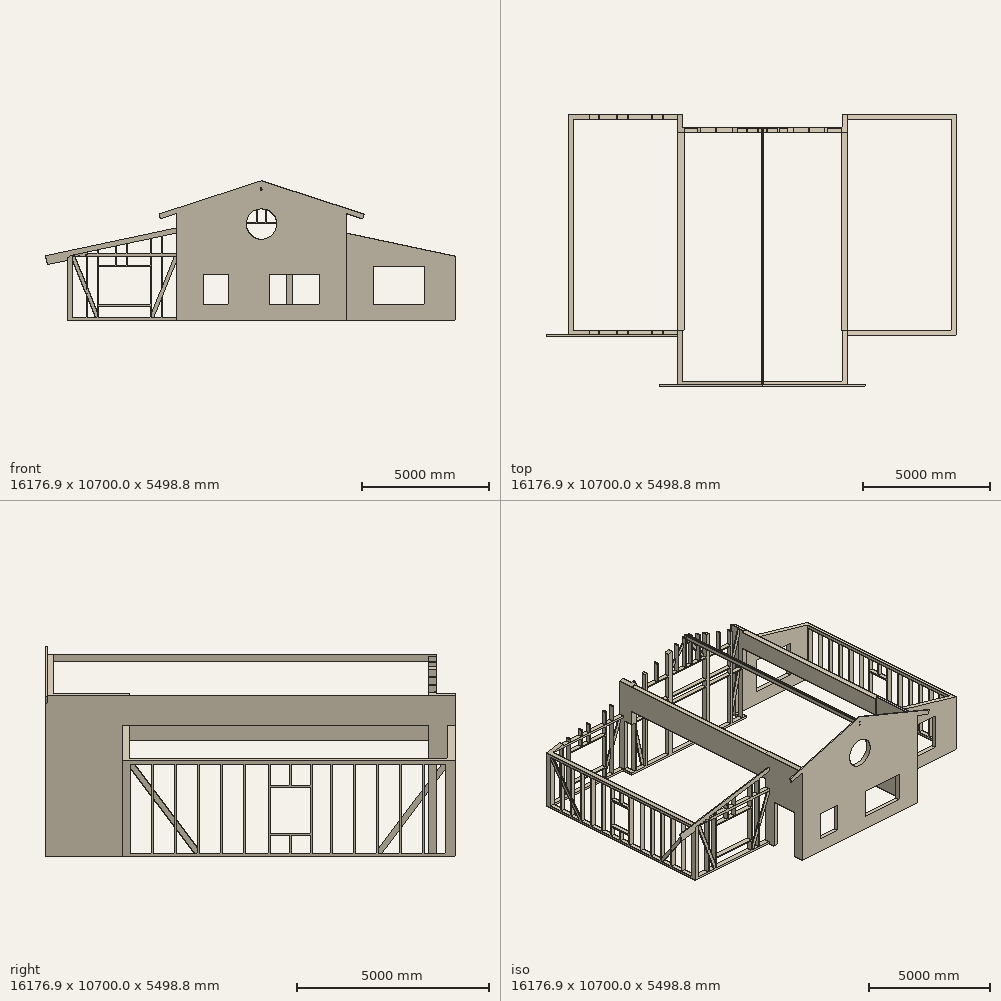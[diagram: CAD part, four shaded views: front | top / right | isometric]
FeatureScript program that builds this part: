
annotation { "Feature Type Name" : "Feature", "Feature Type Description" : "" }
export const myFeature = defineFeature(function(context is Context, id is Id, definition is map)
    precondition{}
    {
        {
            var Q0;
            Q0=qCreatedBy(makeId("Top.planeOp"),FACE);
            var sketch = newSketch(context, id + "F0", { "sketchPlane" : qUnion([Q0])});
            skLineSegment(sketch, "E0.bottom", {"start": v(-3150, 4900) * mm, "end": v(3150, 4900) * mm});
            skLineSegment(sketch, "E0.top", {"start": v(-3150, -4900) * mm, "end": v(3150, -4900) * mm});
            skPoint(sketch, "E0.middle", {"position": v(0, 0) * mm});
            skLineSegment(sketch, "E1.bottom", {"start": v(-3150, 5100) * mm, "end": v(3150, 5100) * mm});
            skLineSegment(sketch, "E1.top", {"start": v(-3350, -5100) * mm, "end": v(3350, -5100) * mm});
            skLineSegment(sketch, "E1.right", {"start": v(3350, 5100) * mm, "end": v(3350, 4900) * mm});
            skLineSegment(sketch, "E2.bottom", {"start": v(3350, -2900) * mm, "end": v(7450, -2900) * mm});
            skLineSegment(sketch, "E2.top", {"start": v(3350, 5400) * mm, "end": v(7450, 5400) * mm});
            skLineSegment(sketch, "E2.left", {"start": v(3350, 4900) * mm, "end": v(3350, 5400) * mm});
            skLineSegment(sketch, "E2.right", {"start": v(7450, -2900) * mm, "end": v(7450, 5400) * mm});
            skLineSegment(sketch, "E3.bottom", {"start": v(3350, -3100) * mm, "end": v(7650, -3100) * mm});
            skLineSegment(sketch, "E3.top", {"start": v(3150, 5600) * mm, "end": v(7650, 5600) * mm});
            skLineSegment(sketch, "E3.right", {"start": v(7650, -3100) * mm, "end": v(7650, 5600) * mm});
            skLineSegment(sketch, "E4.top", {"start": v(-3350, 5400) * mm, "end": v(-7450, 5400) * mm});
            skLineSegment(sketch, "E4.right", {"start": v(-7450, -2900) * mm, "end": v(-7450, 5400) * mm});
            skLineSegment(sketch, "E5.bottom", {"start": v(-3350, -3125) * mm, "end": v(-7650, -3125) * mm});
            skLineSegment(sketch, "E5.top", {"start": v(-3350, 5600) * mm, "end": v(-7650, 5600) * mm});
            skLineSegment(sketch, "E5.left", {"start": v(-3350, 4900) * mm, "end": v(-3350, 5100) * mm});
            skLineSegment(sketch, "E5.right", {"start": v(-7650, -3125) * mm, "end": v(-7650, 5600) * mm});
            skLineSegment(sketch, "E6.bottom", {"start": v(-3350, 5600) * mm, "end": v(-3150, 5600) * mm});
            skLineSegment(sketch, "E6.left", {"start": v(-3350, 5400) * mm, "end": v(-3350, 5100) * mm});
            skLineSegment(sketch, "E6.right", {"start": v(-3150, 5600) * mm, "end": v(-3150, 5100) * mm});
            skLineSegment(sketch, "E7.trimOffspring", {"start": v(3150, 5100) * mm, "end": v(3150, 5600) * mm});
            skLineSegment(sketch, "E8.trimOffspring", {"start": v(3350, -3100) * mm, "end": v(3350, -5100) * mm});
            skLineSegment(sketch, "E9.trimOffspring", {"start": v(-3350, -3125) * mm, "end": v(-3350, -5100) * mm});
            skLineSegment(sketch, "E10", {"start": v(-3350, -2900) * mm, "end": v(-7450, -2900) * mm});
            skLineSegment(sketch, "E11", {"start": v(-3350, 4900) * mm, "end": v(-3150, 4900) * mm});
            skLineSegment(sketch, "E12", {"start": v(3150, 4900) * mm, "end": v(3350, 4900) * mm});
            skLineSegment(sketch, "E13", {"start": v(-3350, -2900) * mm, "end": v(-3150, -2900) * mm});
            skLineSegment(sketch, "E14", {"start": v(-3150, -2900) * mm, "end": v(-3150, -4900) * mm});
            skLineSegment(sketch, "E15", {"start": v(3150, -4900) * mm, "end": v(3150, -2900) * mm});
            skLineSegment(sketch, "E16", {"start": v(3150, -2900) * mm, "end": v(3350, -2900) * mm});
            skSolve(sketch);
        }
        {
            var Q0;
            Q0=qSketchRegion(id+"F0",true);
            extrude(context, id + "F1", {"entities" : qUnion([Q0]), "depth" : 5330 * mm});
        }
        {
            var Q0;
            Q0=makeQuery(id+"F1.opExtrude","SWEPT_FACE",FACE,{"disambiguationData":[OSD([sQuery(id+"F0.wireOp",EDGE,"E1.top")])]});
            var sketch = newSketch(context, id + "F2", { "sketchPlane" : qUnion([Q0])});
            skLineSegment(sketch, "E17.top", {"start": v(0, 6465.16) * mm, "end": v(-7750, 6465.16) * mm});
            skLineSegment(sketch, "E17.left", {"start": v(0, 5288.48) * mm, "end": v(0, 5330) * mm});
            skLineSegment(sketch, "E17.right", {"start": v(-7750, 2500) * mm, "end": v(-7750, 6465.16) * mm});
            skLineSegment(sketch, "E18.top", {"start": v(0, 6465.16) * mm, "end": v(7750, 6465.16) * mm});
            skLineSegment(sketch, "E18.right", {"start": v(7750, 2500) * mm, "end": v(7750, 6465.16) * mm});
            skLineSegment(sketch, "E19.bottom", {"start": v(0, 0) * mm, "end": v(-3350, 0) * mm});
            skLineSegment(sketch, "E19.right", {"start": v(-3350, 3435.25) * mm, "end": v(-3350, 4200) * mm});
            skLineSegment(sketch, "E20.right", {"start": v(3350, 3435.25) * mm, "end": v(3350, 4200) * mm});
            skLineSegment(sketch, "E21", {"start": v(-3350, 4200) * mm, "end": v(0, 5288.48) * mm});
            skLineSegment(sketch, "E22", {"start": v(0, 5288.48) * mm, "end": v(3350, 4200) * mm});
            skPoint(sketch, "E23.orphan", {"position": v(-7750, 0) * mm});
            skLineSegment(sketch, "E24", {"start": v(-7750, 2500) * mm, "end": v(-3350, 3435.25) * mm});
            skLineSegment(sketch, "E25", {"start": v(3350, 3435.25) * mm, "end": v(7750, 2500) * mm});
            skPoint(sketch, "E26.orphan", {"position": v(-7750, 2100) * mm});
            skPoint(sketch, "E27.orphan", {"position": v(-3350, 3024.62) * mm});
            skPoint(sketch, "E28.orphan", {"position": v(7750, 2100) * mm});
            skPoint(sketch, "E29.orphan", {"position": v(3350, 3024.62) * mm});
            skSolve(sketch);
        }
        {
            var Q0;
            Q0=qSketchRegion(id+"F2",true);
            extrude(context, id + "F3", {"entities" : qUnion([Q0]), "operationType" : NewBodyOperationType.REMOVE, "endBound" : BoundingType.THROUGH_ALL, "oppositeDirection" : true, "depth" : 25 * mm});
        }
        {
            var Q0;
            Q0=makeQuery(id+"F3.boolean.opBoolean","MERGE",FACE,{"derivedFrom":[makeQuery(id+"F1.opExtrude","SWEPT_FACE",FACE,{"disambiguationData":[OSD([sQuery(id+"F0.wireOp",EDGE,"E5.left"),sQuery(id+"F0.wireOp",EDGE,"E6.left")])]}),makeQuery(id+"F3.opExtrude","SWEPT_FACE",FACE,{"disambiguationData":[OSD([sQuery(id+"F2.wireOp",EDGE,"E19.right")])]})]});
            var sketch = newSketch(context, id + "F4", { "sketchPlane" : qUnion([Q0])});
            skLineSegment(sketch, "E30.bottom", {"start": v(-4900, 4200) * mm, "end": v(2900, 4200) * mm});
            skLineSegment(sketch, "E30.left", {"start": v(-4900, 4200) * mm, "end": v(-4900, 3147.99) * mm});
            skLineSegment(sketch, "E30.right", {"start": v(2900, 4200) * mm, "end": v(2900, 3147.99) * mm});
            skLineSegment(sketch, "E31.right", {"start": v(-4900, 3024.62) * mm, "end": v(-4900, 3147.99) * mm});
            skLineSegment(sketch, "E32.bottom", {"start": v(-4900, 3024.62) * mm, "end": v(2900, 3024.62) * mm});
            skLineSegment(sketch, "E32.right", {"start": v(2900, 3024.62) * mm, "end": v(2900, 3147.99) * mm});
            skSolve(sketch);
        }
        {
            var Q0;
            Q0=qSketchRegion(id+"F4",true);
            extrude(context, id + "F5", {"entities" : qUnion([Q0]), "operationType" : NewBodyOperationType.ADD, "oppositeDirection" : true, "depth" : 250 * mm});
        }
        {
            var Q0;
            Q0=makeQuery(id+"F3.boolean.opBoolean","MERGE",FACE,{"derivedFrom":[makeQuery(id+"F1.opExtrude","SWEPT_FACE",FACE,{"disambiguationData":[OSD([sQuery(id+"F0.wireOp",EDGE,"E8.trimOffspring")])]}),makeQuery(id+"F3.opExtrude","SWEPT_FACE",FACE,{"disambiguationData":[OSD([sQuery(id+"F2.wireOp",EDGE,"E20.right")])]})]});
            var sketch = newSketch(context, id + "F6", { "sketchPlane" : qUnion([Q0])});
            skLineSegment(sketch, "E33.bottom", {"start": v(-2900, 4200) * mm, "end": v(4900, 4200) * mm});
            skLineSegment(sketch, "E33.top", {"start": v(-2900, 3435.25) * mm, "end": v(4900, 3435.25) * mm});
            skLineSegment(sketch, "E33.left", {"start": v(-2900, 4200) * mm, "end": v(-2900, 3435.25) * mm});
            skLineSegment(sketch, "E33.right", {"start": v(4900, 4200) * mm, "end": v(4900, 3435.25) * mm});
            skSolve(sketch);
        }
        {
            var Q0;
            Q0=qSketchRegion(id+"F6",true);
            extrude(context, id + "F7", {"entities" : qUnion([Q0]), "operationType" : NewBodyOperationType.ADD, "oppositeDirection" : true, "depth" : 250 * mm});
        }
        {
            var Q0;
            Q0=makeQuery(id+"F1.opExtrude","SWEPT_FACE",FACE,{"disambiguationData":[OSD([sQuery(id+"F0.wireOp",EDGE,"E5.bottom")])]});
            var sketch = newSketch(context, id + "F8", { "sketchPlane" : qUnion([Q0])});
            skLineSegment(sketch, "E34.bottom", {"start": v(-6420, 2100) * mm, "end": v(-4380, 2100) * mm});
            skLineSegment(sketch, "E34.top", {"start": v(-6420, 600) * mm, "end": v(-4380, 600) * mm});
            skLineSegment(sketch, "E34.left", {"start": v(-6420, 2100) * mm, "end": v(-6420, 600) * mm});
            skLineSegment(sketch, "E34.right", {"start": v(-4380, 2100) * mm, "end": v(-4380, 600) * mm});
            skLineSegment(sketch, "E35.bottom", {"start": v(4420, 2100) * mm, "end": v(6420, 2100) * mm});
            skLineSegment(sketch, "E35.top", {"start": v(4420, 600) * mm, "end": v(6420, 600) * mm});
            skLineSegment(sketch, "E35.left", {"start": v(4420, 2100) * mm, "end": v(4420, 600) * mm});
            skLineSegment(sketch, "E35.right", {"start": v(6420, 2100) * mm, "end": v(6420, 600) * mm});
            skSolve(sketch);
        }
        {
            var Q0;
            Q0=qSketchRegion(id+"F8",true);
            extrude(context, id + "F9", {"entities" : qUnion([Q0]), "operationType" : NewBodyOperationType.REMOVE, "endBound" : BoundingType.THROUGH_ALL, "oppositeDirection" : true, "depth" : 25 * mm});
        }
        {
            var Q0;
            {var subQ0=makeQuery(id+"F3.opExtrude","SWEPT_FACE",FACE,{"disambiguationData":[OSD([sQuery(id+"F2.wireOp",EDGE,"E19.right")])]});Q0=makeQuery(id+"F5.boolean.opBoolean","MERGE",FACE,{"derivedFrom":[makeQuery(id+"F3.boolean.opBoolean","MERGE",FACE,{"derivedFrom":[makeQuery(id+"F1.opExtrude","SWEPT_FACE",FACE,{"disambiguationData":[OSD([sQuery(id+"F0.wireOp",EDGE,"E5.left"),sQuery(id+"F0.wireOp",EDGE,"E6.left")])]}),subQ0]}),makeQuery(id+"F3.boolean.opBoolean","MERGE",FACE,{"derivedFrom":[makeQuery(id+"F1.opExtrude","SWEPT_FACE",FACE,{"disambiguationData":[OSD([sQuery(id+"F0.wireOp",EDGE,"E9.trimOffspring")])]}),subQ0]}),makeQuery(id+"F5.opExtrude","CAP_FACE",FACE,{"disambiguationData":[OSD([sQuery(id+"F4.wireOp",EDGE,"E30.bottom"),sQuery(id+"F4.wireOp",EDGE,"E30.left"),sQuery(id+"F4.wireOp",EDGE,"E30.right"),sQuery(id+"F4.wireOp",EDGE,"E32.bottom"),sQuery(id+"F4.wireOp",EDGE,"E31.right"),sQuery(id+"F4.wireOp",EDGE,"E32.right")])],"isStart":true})]});}
            var sketch = newSketch(context, id + "F10", { "sketchPlane" : qUnion([Q0])});
            skLineSegment(sketch, "E36.bottom", {"start": v(4625, 0) * mm, "end": v(3425, 0) * mm});
            skLineSegment(sketch, "E36.top", {"start": v(4625, 2100) * mm, "end": v(3425, 2100) * mm});
            skLineSegment(sketch, "E36.left", {"start": v(4625, 0) * mm, "end": v(4625, 2100) * mm});
            skLineSegment(sketch, "E36.right", {"start": v(3425, 0) * mm, "end": v(3425, 2100) * mm});
            skSolve(sketch);
        }
        {
            var Q0;
            Q0=qSketchRegion(id+"F10",true);
            extrude(context, id + "F11", {"entities" : qUnion([Q0]), "operationType" : NewBodyOperationType.REMOVE, "oppositeDirection" : true, "depth" : 250 * mm});
        }
        {
            var Q0;
            Q0=makeQuery(id+"F1.opExtrude","SWEPT_FACE",FACE,{"disambiguationData":[OSD([sQuery(id+"F0.wireOp",EDGE,"E1.top")])]});
            var sketch = newSketch(context, id + "F12", { "sketchPlane" : qUnion([Q0])});
            skLineSegment(sketch, "E37.bottom", {"start": v(300, 1800) * mm, "end": v(2300, 1800) * mm});
            skLineSegment(sketch, "E37.top", {"start": v(300, 600) * mm, "end": v(2300, 600) * mm});
            skLineSegment(sketch, "E37.left", {"start": v(300, 1800) * mm, "end": v(300, 600) * mm});
            skLineSegment(sketch, "E37.right", {"start": v(2300, 1800) * mm, "end": v(2300, 600) * mm});
            skLineSegment(sketch, "E38.bottom", {"start": v(-1300, 600) * mm, "end": v(-2300, 600) * mm});
            skLineSegment(sketch, "E38.top", {"start": v(-1300, 1800) * mm, "end": v(-2300, 1800) * mm});
            skLineSegment(sketch, "E38.left", {"start": v(-1300, 600) * mm, "end": v(-1300, 1800) * mm});
            skLineSegment(sketch, "E38.right", {"start": v(-2300, 600) * mm, "end": v(-2300, 1800) * mm});
            skArc(sketch, "E39", {"start": v(-50, 4387.92) * mm, "mid": v(-424.26, 4214.27) * mm, "end": v(-597.91, 3840) * mm});
            skPoint(sketch, "E40.orphan", {"position": v(-1581.41, 3840) * mm});
            skPoint(sketch, "E41.orphan", {"position": v(-1581.41, 3740) * mm});
            skPoint(sketch, "E42.right.end.orphan", {"position": v(1581.41, 3840) * mm});
            skPoint(sketch, "E42.right.start.orphan", {"position": v(1581.41, 3740) * mm});
            skPoint(sketch, "E43.orphan", {"position": v(-50, 2853.08) * mm});
            skPoint(sketch, "E44.orphan", {"position": v(50, 2853.08) * mm});
            skPoint(sketch, "E45.orphan", {"position": v(-50, 4726.93) * mm});
            skPoint(sketch, "E46.orphan", {"position": v(50, 4726.93) * mm});
            skArc(sketch, "E47.trimOffspring", {"start": v(-597.91, 3740) * mm, "mid": v(-424.26, 3365.74) * mm, "end": v(-50, 3192.09) * mm});
            skArc(sketch, "E48.trimOffspring", {"start": v(597.91, 3840) * mm, "mid": v(424.26, 4214.27) * mm, "end": v(50, 4387.92) * mm});
            skArc(sketch, "E49.trimOffspring", {"start": v(50, 3192.09) * mm, "mid": v(424.26, 3365.74) * mm, "end": v(597.91, 3740) * mm});
            skCircle(sketch, "E50", {"center": v(0, 3790) * mm, "radius": 600 * mm});
            skSolve(sketch);
        }
        {
            var Q0;
            Q0=qSketchRegion(id+"F12",true);
            extrude(context, id + "F13", {"entities" : qUnion([Q0]), "operationType" : NewBodyOperationType.REMOVE, "oppositeDirection" : true, "depth" : 250 * mm});
        }
        {
            var Q0;
            Q0=makeQuery(id+"F1.opExtrude","SWEPT_FACE",FACE,{"disambiguationData":[OSD([sQuery(id+"F0.wireOp",EDGE,"E1.bottom")])]});
            var sketch = newSketch(context, id + "F14", { "sketchPlane" : qUnion([Q0])});
            skLineSegment(sketch, "E51.bottom", {"start": v(-1000, 0) * mm, "end": v(1000, 0) * mm});
            skLineSegment(sketch, "E51.top", {"start": v(-1000, 2400) * mm, "end": v(1000, 2400) * mm});
            skLineSegment(sketch, "E51.left", {"start": v(-1000, 0) * mm, "end": v(-1000, 2400) * mm});
            skLineSegment(sketch, "E51.right", {"start": v(1000, 0) * mm, "end": v(1000, 2400) * mm});
            skPoint(sketch, "E51.middle", {"position": v(0, 1200) * mm});
            skLineSegment(sketch, "E52.bottom", {"start": v(1200, 2400) * mm, "end": v(2450, 2400) * mm});
            skLineSegment(sketch, "E52.top", {"start": v(1200, 0) * mm, "end": v(2450, 0) * mm});
            skLineSegment(sketch, "E52.left", {"start": v(1200, 2400) * mm, "end": v(1200, 0) * mm});
            skLineSegment(sketch, "E52.right", {"start": v(2450, 2400) * mm, "end": v(2450, 0) * mm});
            skLineSegment(sketch, "E53.bottom", {"start": v(-1200, 2400) * mm, "end": v(-2450, 2400) * mm});
            skLineSegment(sketch, "E53.top", {"start": v(-1200, 0) * mm, "end": v(-2450, 0) * mm});
            skLineSegment(sketch, "E53.left", {"start": v(-1200, 2400) * mm, "end": v(-1200, 0) * mm});
            skLineSegment(sketch, "E53.right", {"start": v(-2450, 2400) * mm, "end": v(-2450, 0) * mm});
            skLineSegment(sketch, "E54.bottom", {"start": v(-2450, 2800) * mm, "end": v(-1200, 2800) * mm});
            skLineSegment(sketch, "E54.top", {"start": v(-2450, 3800) * mm, "end": v(-1200, 3800) * mm});
            skLineSegment(sketch, "E54.left", {"start": v(-2450, 2800) * mm, "end": v(-2450, 3800) * mm});
            skLineSegment(sketch, "E54.right", {"start": v(-1200, 2800) * mm, "end": v(-1200, 3800) * mm});
            skLineSegment(sketch, "E55.bottom", {"start": v(-1000, 2800) * mm, "end": v(1000, 2800) * mm});
            skLineSegment(sketch, "E55.top", {"start": v(-1000, 3800) * mm, "end": v(1000, 3800) * mm});
            skLineSegment(sketch, "E55.left", {"start": v(-1000, 2800) * mm, "end": v(-1000, 3800) * mm});
            skLineSegment(sketch, "E55.right", {"start": v(1000, 2800) * mm, "end": v(1000, 3800) * mm});
            skLineSegment(sketch, "E56.bottom", {"start": v(1200, 2800) * mm, "end": v(2450, 2800) * mm});
            skLineSegment(sketch, "E56.top", {"start": v(1200, 3800) * mm, "end": v(2450, 3800) * mm});
            skLineSegment(sketch, "E56.left", {"start": v(1200, 2800) * mm, "end": v(1200, 3800) * mm});
            skLineSegment(sketch, "E56.right", {"start": v(2450, 2800) * mm, "end": v(2450, 3800) * mm});
            skSolve(sketch);
        }
        {
            var Q0;
            Q0=qSketchRegion(id+"F14",true);
            extrude(context, id + "F15", {"entities" : qUnion([Q0]), "operationType" : NewBodyOperationType.REMOVE, "oppositeDirection" : true, "depth" : 250 * mm});
        }
        {
            var Q0;
            Q0=makeQuery(id+"F1.opExtrude","SWEPT_FACE",FACE,{"disambiguationData":[OSD([sQuery(id+"F0.wireOp",EDGE,"E3.right")])]});
            var sketch = newSketch(context, id + "F16", { "sketchPlane" : qUnion([Q0])});
            skLineSegment(sketch, "E57.bottom", {"start": v(772.72, 1800) * mm, "end": v(1812.72, 1800) * mm});
            skLineSegment(sketch, "E57.top", {"start": v(772.72, 600) * mm, "end": v(1812.72, 600) * mm});
            skLineSegment(sketch, "E57.left", {"start": v(772.72, 1800) * mm, "end": v(772.72, 600) * mm});
            skLineSegment(sketch, "E57.right", {"start": v(1812.72, 1800) * mm, "end": v(1812.72, 600) * mm});
            skSolve(sketch);
        }
        {
            var Q0;
            Q0=qSketchRegion(id+"F16",true);
            extrude(context, id + "F17", {"entities" : qUnion([Q0]), "operationType" : NewBodyOperationType.REMOVE, "endBound" : BoundingType.THROUGH_ALL, "oppositeDirection" : true, "depth" : 25 * mm});
        }
        {
            var Q0;
            Q0=makeQuery(id+"F1.opExtrude","SWEPT_FACE",FACE,{"disambiguationData":[OSD([sQuery(id+"F0.wireOp",EDGE,"E5.bottom")])]});
            var sketch = newSketch(context, id + "F18", { "sketchPlane" : qUnion([Q0])});
            skLineSegment(sketch, "E58", {"start": v(-3350, 3435.25) * mm, "end": v(-8485.27, 2343.71) * mm});
            skLineSegment(sketch, "E59", {"start": v(-8485.27, 2343.71) * mm, "end": v(-8526.86, 2539.34) * mm});
            skLineSegment(sketch, "E60", {"start": v(-8526.86, 2539.34) * mm, "end": v(-3350, 3639.72) * mm});
            skLineSegment(sketch, "E61", {"start": v(-3350, 3639.72) * mm, "end": v(-3350, 3435.25) * mm});
            skLineSegment(sketch, "E62", {"start": v(-8485.27, 2343.71) * mm, "end": v(-8452, 2187.2) * mm});
            skLineSegment(sketch, "E63", {"start": v(-8452, 2187.2) * mm, "end": v(-3350, 3271.67) * mm});
            skLineSegment(sketch, "E64", {"start": v(-3350, 3271.67) * mm, "end": v(-3350, 3435.25) * mm});
            skSolve(sketch);
        }
        {
            var Q0;
            Q0=qSketchRegion(id+"F18",true);
            extrude(context, id + "F19", {"entities" : qUnion([Q0]), "oppositeDirection" : true, "depth" : 50 * mm});
        }
        {
            var Q0;
            Q0=makeQuery(id+"F3.boolean.opBoolean","COPY",FACE,{"disambiguationData":[TD([makeQuery(id+"F1.opExtrude","SWEPT_FACE",FACE,{"disambiguationData":[OSD([sQuery(id+"F0.wireOp",EDGE,"E0.top")])]})])],"derivedFrom":makeQuery(id+"F3.opExtrude","SWEPT_FACE",FACE,{"disambiguationData":[OSD([sQuery(id+"F2.wireOp",EDGE,"E21")])]})});
            var sketch = newSketch(context, id + "F20", { "sketchPlane" : qUnion([Q0])});
            skPoint(sketch, "E65.right.end.orphan", {"position": v(-2565.77, -4900) * mm});
            skLineSegment(sketch, "E66.bottom", {"start": v(1634.23, -5100) * mm, "end": v(-2565.77, -5100) * mm});
            skLineSegment(sketch, "E66.top", {"start": v(1634.23, -5050) * mm, "end": v(-2565.77, -5050) * mm});
            skLineSegment(sketch, "E66.left", {"start": v(1634.23, -5100) * mm, "end": v(1634.23, -5050) * mm});
            skLineSegment(sketch, "E66.right", {"start": v(-2565.77, -5100) * mm, "end": v(-2565.77, -5050) * mm});
            skSolve(sketch);
        }
        {
            var Q0;
            Q0=qSketchRegion(id+"F20",true);
            extrude(context, id + "F21", {"entities" : qUnion([Q0]), "depth" : 200 * mm});
        }
        {
            var Q0;
            Q0=makeQuery(id+"F3.boolean.opBoolean","COPY",FACE,{"disambiguationData":[TD([makeQuery(id+"F1.opExtrude","SWEPT_FACE",FACE,{"disambiguationData":[OSD([sQuery(id+"F0.wireOp",EDGE,"E0.top")])]})])],"derivedFrom":makeQuery(id+"F3.opExtrude","SWEPT_FACE",FACE,{"disambiguationData":[OSD([sQuery(id+"F2.wireOp",EDGE,"E22")])]})});
            var sketch = newSketch(context, id + "F22", { "sketchPlane" : qUnion([Q0])});
            skLineSegment(sketch, "E67.bottom", {"start": v(-1634.23, -5100) * mm, "end": v(2565.77, -5100) * mm});
            skLineSegment(sketch, "E67.top", {"start": v(-1634.23, -5050) * mm, "end": v(2565.77, -5050) * mm});
            skLineSegment(sketch, "E67.left", {"start": v(-1634.23, -5100) * mm, "end": v(-1634.23, -5050) * mm});
            skLineSegment(sketch, "E67.right", {"start": v(2565.77, -5100) * mm, "end": v(2565.77, -5050) * mm});
            skSolve(sketch);
        }
        {
            var Q0;
            Q0=qSketchRegion(id+"F22",true);
            extrude(context, id + "F23", {"entities" : qUnion([Q0]), "depth" : 200 * mm});
        }
        {
            var Q0;
            Q0=makeQuery(id+"F1.opExtrude","SWEPT_FACE",FACE,{"disambiguationData":[OSD([sQuery(id+"F0.wireOp",EDGE,"E5.right")])]});
            var sketch = newSketch(context, id + "F24", { "sketchPlane" : qUnion([Q0])});
            skLineSegment(sketch, "E68.bottom", {"start": v(-5350, 2421.26) * mm, "end": v(-4800, 2421.26) * mm});
            skLineSegment(sketch, "E68.top", {"start": v(-5350, 100) * mm, "end": v(-4800, 100) * mm});
            skLineSegment(sketch, "E68.left", {"start": v(-5350, 2421.26) * mm, "end": v(-5350, 100) * mm});
            skLineSegment(sketch, "E68.right", {"start": v(-1862.72, 2421.26) * mm, "end": v(-1862.72, 100) * mm});
            skPoint(sketch, "E69.firstSnap0", {"position": v(-3606.36, 2421.26) * mm});
            skLineSegment(sketch, "E69.bottom", {"start": v(-722.72, 2421.26) * mm, "end": v(-125, 2421.26) * mm});
            skLineSegment(sketch, "E69.top", {"start": v(-722.72, 100) * mm, "end": v(-125, 100) * mm});
            skLineSegment(sketch, "E69.left", {"start": v(-722.72, 2421.26) * mm, "end": v(-722.72, 100) * mm});
            skLineSegment(sketch, "E69.right", {"start": v(2875, 2421.26) * mm, "end": v(2875, 100) * mm});
            skLineSegment(sketch, "E70.bottom", {"start": v(-1812.72, 2421.26) * mm, "end": v(-1317.72, 2421.26) * mm});
            skLineSegment(sketch, "E70.top", {"start": v(-1812.72, 1850) * mm, "end": v(-1317.72, 1850) * mm});
            skLineSegment(sketch, "E70.left", {"start": v(-1812.72, 2421.26) * mm, "end": v(-1812.72, 1850) * mm});
            skLineSegment(sketch, "E70.right", {"start": v(-772.72, 2421.26) * mm, "end": v(-772.72, 1850) * mm});
            skLineSegment(sketch, "E71.bottom", {"start": v(-1812.72, 550) * mm, "end": v(-1317.72, 550) * mm});
            skLineSegment(sketch, "E71.top", {"start": v(-1812.72, 100) * mm, "end": v(-1317.72, 100) * mm});
            skLineSegment(sketch, "E71.left", {"start": v(-1812.72, 550) * mm, "end": v(-1812.72, 100) * mm});
            skLineSegment(sketch, "E71.right", {"start": v(-772.72, 550) * mm, "end": v(-772.72, 100) * mm});
            skLineSegment(sketch, "E72.left", {"start": v(-4800, 2421.26) * mm, "end": v(-4800, 100) * mm});
            skLineSegment(sketch, "E72.right", {"start": v(-4750, 2421.26) * mm, "end": v(-4750, 100) * mm});
            skLineSegment(sketch, "E73.left", {"start": v(-4200, 2421.26) * mm, "end": v(-4200, 100) * mm});
            skLineSegment(sketch, "E73.right", {"start": v(-4150, 2421.26) * mm, "end": v(-4150, 100) * mm});
            skLineSegment(sketch, "E74.bottom", {"start": v(-3606.36, 2421.26) * mm, "end": v(-3600, 2421.26) * mm});
            skLineSegment(sketch, "E74.left", {"start": v(-3600, 2421.26) * mm, "end": v(-3600, 100) * mm});
            skLineSegment(sketch, "E74.right", {"start": v(-3550, 2421.26) * mm, "end": v(-3550, 100) * mm});
            skLineSegment(sketch, "E75.left", {"start": v(-3000, 2421.26) * mm, "end": v(-3000, 100) * mm});
            skLineSegment(sketch, "E75.right", {"start": v(-2950, 2421.26) * mm, "end": v(-2950, 100) * mm});
            skLineSegment(sketch, "E76.left", {"start": v(-2400, 2421.26) * mm, "end": v(-2400, 100) * mm});
            skLineSegment(sketch, "E76.right", {"start": v(-2350, 2421.26) * mm, "end": v(-2350, 100) * mm});
            skLineSegment(sketch, "E77.trimOffspring", {"start": v(-4750, 2421.26) * mm, "end": v(-4200, 2421.26) * mm});
            skLineSegment(sketch, "E78.trimOffspring", {"start": v(-4150, 2421.26) * mm, "end": v(-3606.36, 2421.26) * mm});
            skLineSegment(sketch, "E79.trimOffspring", {"start": v(-3550, 2421.26) * mm, "end": v(-3000, 2421.26) * mm});
            skLineSegment(sketch, "E80.trimOffspring", {"start": v(-2950, 2421.26) * mm, "end": v(-2400, 2421.26) * mm});
            skLineSegment(sketch, "E81.trimOffspring", {"start": v(-2350, 2421.26) * mm, "end": v(-1862.72, 2421.26) * mm});
            skLineSegment(sketch, "E82.trimOffspring", {"start": v(-4750, 100) * mm, "end": v(-4200, 100) * mm});
            skLineSegment(sketch, "E83.trimOffspring", {"start": v(-4150, 100) * mm, "end": v(-3600, 100) * mm});
            skLineSegment(sketch, "E84.trimOffspring", {"start": v(-3550, 100) * mm, "end": v(-3000, 100) * mm});
            skLineSegment(sketch, "E85.trimOffspring", {"start": v(-2950, 100) * mm, "end": v(-2400, 100) * mm});
            skLineSegment(sketch, "E86.trimOffspring", {"start": v(-2350, 100) * mm, "end": v(-1862.72, 100) * mm});
            skLineSegment(sketch, "E87.left", {"start": v(-125, 2421.26) * mm, "end": v(-125, 100) * mm});
            skLineSegment(sketch, "E87.right", {"start": v(-75, 2421.26) * mm, "end": v(-75, 100) * mm});
            skLineSegment(sketch, "E88.left", {"start": v(475, 2421.26) * mm, "end": v(475, 100) * mm});
            skLineSegment(sketch, "E88.right", {"start": v(525, 2421.26) * mm, "end": v(525, 100) * mm});
            skLineSegment(sketch, "E89.left", {"start": v(1075, 2421.26) * mm, "end": v(1075, 100) * mm});
            skLineSegment(sketch, "E89.right", {"start": v(1125, 2421.26) * mm, "end": v(1125, 100) * mm});
            skLineSegment(sketch, "E90.left", {"start": v(1675, 2421.26) * mm, "end": v(1675, 100) * mm});
            skLineSegment(sketch, "E90.right", {"start": v(1725, 2421.26) * mm, "end": v(1725, 100) * mm});
            skLineSegment(sketch, "E91.left", {"start": v(2275, 2421.26) * mm, "end": v(2275, 100) * mm});
            skLineSegment(sketch, "E91.right", {"start": v(2325, 2421.26) * mm, "end": v(2325, 100) * mm});
            skLineSegment(sketch, "E92.trimOffspring", {"start": v(525, 2421.26) * mm, "end": v(1075, 2421.26) * mm});
            skLineSegment(sketch, "E93.trimOffspring", {"start": v(-75, 2421.26) * mm, "end": v(475, 2421.26) * mm});
            skLineSegment(sketch, "E94.trimOffspring", {"start": v(1125, 2421.26) * mm, "end": v(1675, 2421.26) * mm});
            skLineSegment(sketch, "E95.trimOffspring", {"start": v(1725, 2421.26) * mm, "end": v(2275, 2421.26) * mm});
            skLineSegment(sketch, "E96.trimOffspring", {"start": v(2325, 2421.26) * mm, "end": v(2875, 2421.26) * mm});
            skLineSegment(sketch, "E97.trimOffspring", {"start": v(2325, 100) * mm, "end": v(2875, 100) * mm});
            skLineSegment(sketch, "E98.trimOffspring", {"start": v(1725, 100) * mm, "end": v(2275, 100) * mm});
            skLineSegment(sketch, "E99.trimOffspring", {"start": v(1125, 100) * mm, "end": v(1675, 100) * mm});
            skLineSegment(sketch, "E100.trimOffspring", {"start": v(525, 100) * mm, "end": v(1075, 100) * mm});
            skLineSegment(sketch, "E101.trimOffspring", {"start": v(-75, 100) * mm, "end": v(475, 100) * mm});
            skLineSegment(sketch, "E102.left", {"start": v(-1317.72, 550) * mm, "end": v(-1317.72, 100) * mm});
            skLineSegment(sketch, "E102.right", {"start": v(-1267.72, 550) * mm, "end": v(-1267.72, 100) * mm});
            skLineSegment(sketch, "E103.left", {"start": v(-1267.72, 1850) * mm, "end": v(-1267.72, 2421.26) * mm});
            skLineSegment(sketch, "E103.right", {"start": v(-1317.72, 1850) * mm, "end": v(-1317.72, 2421.26) * mm});
            skLineSegment(sketch, "E104.trimOffspring", {"start": v(-1267.72, 2421.26) * mm, "end": v(-772.72, 2421.26) * mm});
            skLineSegment(sketch, "E105.trimOffspring", {"start": v(-1267.72, 1850) * mm, "end": v(-772.72, 1850) * mm});
            skLineSegment(sketch, "E106.trimOffspring", {"start": v(-1267.72, 550) * mm, "end": v(-772.72, 550) * mm});
            skLineSegment(sketch, "E107.trimOffspring", {"start": v(-1267.72, 100) * mm, "end": v(-772.72, 100) * mm});
            skSolve(sketch);
        }
        {
            var Q0;
            Q0 = qSketchRegion(id + "F24", true);
            extrude(context, id + "F25", {"entities" : qUnion([Q0]), "operationType" : NewBodyOperationType.REMOVE, "oppositeDirection" : true, "depth" : 20000 * mm, "offsetDistance" : 25 * mm});
        }
        {
            var Q0;
            Q0=makeQuery(id+"F1.opExtrude","SWEPT_FACE",FACE,{"disambiguationData":[OSD([sQuery(id+"F0.wireOp",EDGE,"E5.bottom")])]});
            var sketch = newSketch(context, id + "F26", { "sketchPlane" : qUnion([Q0])});
            skLineSegment(sketch, "E108.left", {"start": v(-7450, 100) * mm, "end": v(-7450, 2521.26) * mm});
            skLineSegment(sketch, "E109.left", {"start": v(-6900, 100) * mm, "end": v(-6900, 2521.26) * mm});
            skLineSegment(sketch, "E110.left", {"start": v(-6420, 100) * mm, "end": v(-6420, 550) * mm});
            skLineSegment(sketch, "E110.right", {"start": v(-6470, 100) * mm, "end": v(-6470, 2521.26) * mm});
            skLineSegment(sketch, "E111.top", {"start": v(-4380, 5521.4) * mm, "end": v(-4330, 5521.4) * mm});
            skLineSegment(sketch, "E111.left", {"start": v(-4380, 100) * mm, "end": v(-4380, 550) * mm});
            skLineSegment(sketch, "E111.right", {"start": v(-4330, 100) * mm, "end": v(-4330, 2521.26) * mm});
            skLineSegment(sketch, "E112.top", {"start": v(-6420, 2150) * mm, "end": v(-5782.94, 2150) * mm});
            skLineSegment(sketch, "E113.top", {"start": v(-6420, 550) * mm, "end": v(-4380, 550) * mm});
            skLineSegment(sketch, "E114.left", {"start": v(-5782.94, 2150) * mm, "end": v(-5782.94, 2521.26) * mm});
            skLineSegment(sketch, "E114.right", {"start": v(-5732.94, 2150) * mm, "end": v(-5732.94, 2521.26) * mm});
            skLineSegment(sketch, "E115.left", {"start": v(-5335.08, 2150) * mm, "end": v(-5335.08, 2521.26) * mm});
            skLineSegment(sketch, "E115.right", {"start": v(-5285.08, 2150) * mm, "end": v(-5285.08, 2521.26) * mm});
            skLineSegment(sketch, "E116", {"start": v(-7650, 2521.26) * mm, "end": v(-7450, 2563.77) * mm});
            skLineSegment(sketch, "E117", {"start": v(-3350, 3435.25) * mm, "end": v(-3350, 100) * mm});
            skLineSegment(sketch, "E118.top", {"start": v(-7450, 100) * mm, "end": v(-6900, 100) * mm});
            skPoint(sketch, "E110.bottom.start.orphan", {"position": v(-6420, 0) * mm});
            skPoint(sketch, "E118.bottom.start.orphan", {"position": v(-4380, 0) * mm});
            skLineSegment(sketch, "E119.trimOffspring", {"start": v(-4330, 100) * mm, "end": v(-3350, 100) * mm});
            skLineSegment(sketch, "E120.trimOffspring", {"start": v(-6420, 2150) * mm, "end": v(-6420, 2521.26) * mm});
            skLineSegment(sketch, "E121.trimOffspring", {"start": v(-6420, 100) * mm, "end": v(-4380, 100) * mm});
            skLineSegment(sketch, "E122", {"start": v(-6850, 2691.3) * mm, "end": v(-6850, 2621.26) * mm});
            skLineSegment(sketch, "E123.trimOffspring", {"start": v(-6850, 100) * mm, "end": v(-6470, 100) * mm});
            skLineSegment(sketch, "E124.trimOffspring", {"start": v(-6850, 2691.3) * mm, "end": v(-6470, 2772.07) * mm});
            skLineSegment(sketch, "E125.trimOffspring", {"start": v(-6420, 2782.7) * mm, "end": v(-3350, 3435.25) * mm});
            skLineSegment(sketch, "E126", {"start": v(-5782.94, 2918.11) * mm, "end": v(-6420, 2782.7) * mm});
            skLineSegment(sketch, "E127", {"start": v(-5732.94, 2928.74) * mm, "end": v(-5335.08, 3013.3) * mm});
            skLineSegment(sketch, "E128.trimOffspring", {"start": v(-4380, 2150) * mm, "end": v(-4380, 2521.26) * mm});
            skLineSegment(sketch, "E129.trimOffspring", {"start": v(-5732.94, 2150) * mm, "end": v(-5335.08, 2150) * mm});
            skLineSegment(sketch, "E130.trimOffspring", {"start": v(-5285.08, 2150) * mm, "end": v(-4380, 2150) * mm});
            skLineSegment(sketch, "E131.top", {"start": v(-7450, 2521.26) * mm, "end": v(-6900, 2521.26) * mm});
            skLineSegment(sketch, "E131.right", {"start": v(-3350, 2621.26) * mm, "end": v(-3350, 2521.26) * mm});
            skPoint(sketch, "E131.left.start.orphan", {"position": v(-7650, 2621.26) * mm});
            skLineSegment(sketch, "E132.trimOffspring", {"start": v(-6900, 2621.26) * mm, "end": v(-6900, 2680.67) * mm});
            skLineSegment(sketch, "E133.trimOffspring", {"start": v(-6850, 2521.26) * mm, "end": v(-6850, 100) * mm});
            skLineSegment(sketch, "E134.trimOffspring", {"start": v(-6420, 2621.26) * mm, "end": v(-6420, 2782.7) * mm});
            skLineSegment(sketch, "E135.trimOffspring", {"start": v(-6470, 2621.26) * mm, "end": v(-6470, 2772.07) * mm});
            skLineSegment(sketch, "E136.trimOffspring", {"start": v(-6420, 2521.26) * mm, "end": v(-5782.94, 2521.26) * mm});
            skLineSegment(sketch, "E137.trimOffspring", {"start": v(-6850, 2521.26) * mm, "end": v(-6470, 2521.26) * mm});
            skLineSegment(sketch, "E138.trimOffspring", {"start": v(-6850, 2621.26) * mm, "end": v(-6470, 2621.26) * mm});
            skLineSegment(sketch, "E139.trimOffspring", {"start": v(-6420, 2621.26) * mm, "end": v(-5782.94, 2621.26) * mm});
            skLineSegment(sketch, "E140.trimOffspring", {"start": v(-5732.94, 2621.26) * mm, "end": v(-5335.08, 2621.26) * mm});
            skLineSegment(sketch, "E141.trimOffspring", {"start": v(-5732.94, 2521.26) * mm, "end": v(-5335.08, 2521.26) * mm});
            skLineSegment(sketch, "E142.trimOffspring", {"start": v(-5285.08, 2521.26) * mm, "end": v(-4380, 2521.26) * mm});
            skLineSegment(sketch, "E143.trimOffspring", {"start": v(-5285.08, 2621.26) * mm, "end": v(-4380, 2621.26) * mm});
            skLineSegment(sketch, "E144.trimOffspring", {"start": v(-4330, 2521.26) * mm, "end": v(-3950, 2521.26) * mm});
            skLineSegment(sketch, "E145.trimOffspring", {"start": v(-4380, 2621.26) * mm, "end": v(-4380, 3216.32) * mm});
            skLineSegment(sketch, "E146.trimOffspring", {"start": v(-5285.08, 2621.26) * mm, "end": v(-5285.08, 3023.94) * mm});
            skLineSegment(sketch, "E147.trimOffspring", {"start": v(-5335.08, 2621.26) * mm, "end": v(-5335.08, 3013.3) * mm});
            skLineSegment(sketch, "E148.trimOffspring", {"start": v(-5782.94, 2621.26) * mm, "end": v(-5782.94, 2918.11) * mm});
            skLineSegment(sketch, "E149.trimOffspring", {"start": v(-5732.94, 2621.26) * mm, "end": v(-5732.94, 2928.74) * mm});
            skLineSegment(sketch, "E150", {"start": v(-4330, 2621.26) * mm, "end": v(-4330, 3226.94) * mm});
            skLineSegment(sketch, "E151", {"start": v(-4330, 3226.94) * mm, "end": v(-4380, 3216.32) * mm});
            skLineSegment(sketch, "E152.bottom", {"start": v(-3900, 100) * mm, "end": v(-3950, 100) * mm});
            skLineSegment(sketch, "E152.left", {"start": v(-3900, 100) * mm, "end": v(-3900, 2521.26) * mm});
            skLineSegment(sketch, "E152.right", {"start": v(-3950, 100) * mm, "end": v(-3950, 2521.26) * mm});
            skLineSegment(sketch, "E153.trimOffspring", {"start": v(-3900, 2621.26) * mm, "end": v(-3350, 2621.26) * mm});
            skLineSegment(sketch, "E154", {"start": v(-3950, 3307.71) * mm, "end": v(-3900, 3318.34) * mm});
            skLineSegment(sketch, "E155.trimOffspring", {"start": v(-3900, 2621.26) * mm, "end": v(-3900, 3318.34) * mm});
            skLineSegment(sketch, "E156.trimOffspring", {"start": v(-3900, 2521.26) * mm, "end": v(-3350, 2521.26) * mm});
            skLineSegment(sketch, "E157", {"start": v(-4330, 2621.26) * mm, "end": v(-3950, 2621.26) * mm});
            skLineSegment(sketch, "E158", {"start": v(-3950, 2621.26) * mm, "end": v(-3950, 3307.71) * mm});
            skLineSegment(sketch, "E159", {"start": v(-7179.54, 2621.26) * mm, "end": v(-7450, 2621.26) * mm});
            skLineSegment(sketch, "E160", {"start": v(-7450, 2621.26) * mm, "end": v(-7450, 2521.26) * mm});
            skLineSegment(sketch, "E161", {"start": v(-7179.54, 2621.26) * mm, "end": v(-6900, 2680.67) * mm});
            skSolve(sketch);
        }
        {
            var Q0;
            Q0 = qSketchRegion(id + "F26", true);
            extrude(context, id + "F27", {"entities" : qUnion([Q0]), "operationType" : NewBodyOperationType.REMOVE, "oppositeDirection" : true, "depth" : 25000 * mm, "offsetDistance" : 25 * mm});
        }
        {
            var Q0;
            Q0=makeQuery(id+"F1.opExtrude","SWEPT_FACE",FACE,{"disambiguationData":[OSD([sQuery(id+"F0.wireOp",EDGE,"E5.right")])]});
            var sketch = newSketch(context, id + "F28", { "sketchPlane" : qUnion([Q0])});
            skLineSegment(sketch, "E162", {"start": v(1125, 224.59) * mm, "end": v(2781.07, 2421.26) * mm});
            skLineSegment(sketch, "E163", {"start": v(2875, 2296.67) * mm, "end": v(1218.93, 100) * mm});
            skLineSegment(sketch, "E164", {"start": v(1125, 100) * mm, "end": v(1125, 224.59) * mm});
            skLineSegment(sketch, "E165", {"start": v(1125, 100) * mm, "end": v(1218.93, 100) * mm});
            skLineSegment(sketch, "E166", {"start": v(2875, 2421.26) * mm, "end": v(2781.07, 2421.26) * mm});
            skLineSegment(sketch, "E167", {"start": v(2875, 2421.26) * mm, "end": v(2875, 2296.67) * mm});
            skLineSegment(sketch, "E168", {"start": v(-3600, 100) * mm, "end": v(-3693.93, 100) * mm});
            skLineSegment(sketch, "E169", {"start": v(-3693.93, 100) * mm, "end": v(-5350, 2296.67) * mm});
            skLineSegment(sketch, "E170", {"start": v(-5350, 2296.67) * mm, "end": v(-5350, 2421.26) * mm});
            skLineSegment(sketch, "E171", {"start": v(-5350, 2421.26) * mm, "end": v(-5256.07, 2421.26) * mm});
            skLineSegment(sketch, "E172", {"start": v(-5256.07, 2421.26) * mm, "end": v(-3600, 224.59) * mm});
            skLineSegment(sketch, "E173", {"start": v(-3600, 224.59) * mm, "end": v(-3600, 100) * mm});
            skSolve(sketch);
        }
        {
            var Q0;
            Q0 = qSketchRegion(id + "F28", true);
            extrude(context, id + "F29", {"entities" : qUnion([Q0]), "oppositeDirection" : true, "depth" : 50 * mm, "offsetDistance" : 25 * mm});
        }
        {
            var Q0;
            Q0=makeQuery(id+"F1.opExtrude","SWEPT_FACE",FACE,{"disambiguationData":[OSD([sQuery(id+"F0.wireOp",EDGE,"E5.bottom")])]});
            var sketch = newSketch(context, id + "F30", { "sketchPlane" : qUnion([Q0])});
            skLineSegment(sketch, "E174", {"start": v(-7450, 2521.26) * mm, "end": v(-7450, 2321.35) * mm});
            skLineSegment(sketch, "E175", {"start": v(-7450, 2321.35) * mm, "end": v(-6550.91, 100) * mm});
            skLineSegment(sketch, "E176", {"start": v(-6550.91, 100) * mm, "end": v(-6470, 100) * mm});
            skLineSegment(sketch, "E177", {"start": v(-6470, 100) * mm, "end": v(-6470, 299.9) * mm});
            skLineSegment(sketch, "E178", {"start": v(-6470, 299.9) * mm, "end": v(-7369.09, 2521.26) * mm});
            skLineSegment(sketch, "E179", {"start": v(-7369.09, 2521.26) * mm, "end": v(-7450, 2521.26) * mm});
            skLineSegment(sketch, "E180", {"start": v(-3350, 2521.26) * mm, "end": v(-3430.91, 2521.26) * mm});
            skLineSegment(sketch, "E181", {"start": v(-3430.91, 2521.26) * mm, "end": v(-4330, 299.9) * mm});
            skLineSegment(sketch, "E182", {"start": v(-4330, 299.9) * mm, "end": v(-4330, 100) * mm});
            skLineSegment(sketch, "E183", {"start": v(-4330, 100) * mm, "end": v(-4249.09, 100) * mm});
            skLineSegment(sketch, "E184", {"start": v(-4249.09, 100) * mm, "end": v(-3350, 2321.35) * mm});
            skLineSegment(sketch, "E185", {"start": v(-3350, 2321.35) * mm, "end": v(-3350, 2521.26) * mm});
            skSolve(sketch);
        }
        {
            var Q0;
            Q0 = qSketchRegion(id + "F30", true);
            extrude(context, id + "F31", {"entities" : qUnion([Q0]), "oppositeDirection" : true, "depth" : 50 * mm, "offsetDistance" : 25 * mm});
        }
        {
            var Q0;
            {var subQ2=makeQuery(id+"F1.opExtrude","SWEPT_FACE",FACE,{"disambiguationData":[OSD([sQuery(id+"F0.wireOp",EDGE,"E1.bottom")])]});Q0=makeQuery(id+"F25.boolean.opBoolean","SPLIT",FACE,{"disambiguationData":[TD([makeQuery(id+"F15.boolean.opBoolean","COPY",FACE,{"derivedFrom":makeQuery(id+"F15.opExtrude","SWEPT_FACE",FACE,{"disambiguationData":[OSD([sQuery(id+"F14.wireOp",EDGE,"E54.bottom")])]})})])],"derivedFrom":subQ2});}
            var sketch = newSketch(context, id + "F32", { "sketchPlane" : qUnion([Q0])});
            skLineSegment(sketch, "E186.bottom", {"start": v(-3150, 2421.26) * mm, "end": v(3150, 2421.26) * mm});
            skLineSegment(sketch, "E186.top", {"start": v(-3150, 1.26) * mm, "end": v(3150, 1.26) * mm});
            skLineSegment(sketch, "E186.left", {"start": v(-3150, 2421.26) * mm, "end": v(-3150, 1.26) * mm});
            skLineSegment(sketch, "E186.right", {"start": v(3150, 2421.26) * mm, "end": v(3150, 1.26) * mm});
            skSolve(sketch);
        }
        {
            var Q0;
            Q0 = qSketchRegion(id + "F32", true);
            extrude(context, id + "F33", {"entities" : qUnion([Q0]), "operationType" : NewBodyOperationType.ADD, "oppositeDirection" : true, "depth" : 200 * mm, "offsetDistance" : 25 * mm});
        }
        {
            var Q0;
            {var subQ5=sQuery(id+"F0.wireOp",EDGE,"E1.bottom");var subQ6=makeQuery(id+"F1.opExtrude","SWEPT_FACE",FACE,{"disambiguationData":[OSD([subQ5])]});var subQ18=subQ6;Q0=makeQuery(id+"F33.boolean.opBoolean","MERGE",FACE,{"derivedFrom":[makeQuery(id+"F25.boolean.opBoolean","SPLIT",FACE,{"disambiguationData":[TD([makeQuery(id+"F15.boolean.opBoolean","COPY",FACE,{"derivedFrom":makeQuery(id+"F15.opExtrude","SWEPT_FACE",FACE,{"disambiguationData":[OSD([sQuery(id+"F14.wireOp",EDGE,"E52.right")])]})})])],"derivedFrom":subQ18}),makeQuery(id+"F25.boolean.opBoolean","SPLIT",FACE,{"disambiguationData":[TD([makeQuery(id+"F15.boolean.opBoolean","COPY",FACE,{"derivedFrom":makeQuery(id+"F15.opExtrude","SWEPT_FACE",FACE,{"disambiguationData":[OSD([sQuery(id+"F14.wireOp",EDGE,"E53.right")])]})})])],"derivedFrom":subQ18}),makeQuery(id+"F25.boolean.opBoolean","SPLIT",FACE,{"disambiguationData":[TD([makeQuery(id+"F15.boolean.opBoolean","COPY",FACE,{"derivedFrom":makeQuery(id+"F15.opExtrude","SWEPT_FACE",FACE,{"disambiguationData":[OSD([sQuery(id+"F14.wireOp",EDGE,"E54.bottom")])]})})])],"derivedFrom":subQ18}),makeQuery(id+"F33.opExtrude","CAP_FACE",FACE,{"disambiguationData":[OSD([sQuery(id+"F32.wireOp",EDGE,"E186.bottom"),sQuery(id+"F32.wireOp",EDGE,"E186.top"),sQuery(id+"F32.wireOp",EDGE,"E186.left"),sQuery(id+"F32.wireOp",EDGE,"E186.right")])],"isStart":true})]});}
            var sketch = newSketch(context, id + "F34", { "sketchPlane" : qUnion([Q0])});
            skLineSegment(sketch, "E187.bottom", {"start": v(-2450, 2401.26) * mm, "end": v(-1200, 2401.26) * mm});
            skLineSegment(sketch, "E187.top", {"start": v(-2450, 101.26) * mm, "end": v(-1200, 101.26) * mm});
            skLineSegment(sketch, "E187.left", {"start": v(-2450, 2401.26) * mm, "end": v(-2450, 101.26) * mm});
            skLineSegment(sketch, "E187.right", {"start": v(-1200, 2401.26) * mm, "end": v(-1200, 101.26) * mm});
            skLineSegment(sketch, "E188.bottom", {"start": v(-1000, 2401.26) * mm, "end": v(1000, 2401.26) * mm});
            skLineSegment(sketch, "E188.top", {"start": v(-1000, 101.26) * mm, "end": v(1000, 101.26) * mm});
            skLineSegment(sketch, "E188.left", {"start": v(-1000, 2401.26) * mm, "end": v(-1000, 101.26) * mm});
            skLineSegment(sketch, "E188.right", {"start": v(1000, 2401.26) * mm, "end": v(1000, 101.26) * mm});
            skLineSegment(sketch, "E189.bottom", {"start": v(1200, 2401.26) * mm, "end": v(2450, 2401.26) * mm});
            skLineSegment(sketch, "E189.top", {"start": v(1200, 101.26) * mm, "end": v(2450, 101.26) * mm});
            skLineSegment(sketch, "E189.left", {"start": v(1200, 2401.26) * mm, "end": v(1200, 101.26) * mm});
            skLineSegment(sketch, "E189.right", {"start": v(2450, 2401.26) * mm, "end": v(2450, 101.26) * mm});
            skLineSegment(sketch, "E190.bottom", {"start": v(-2550, 2401.26) * mm, "end": v(-3100, 2401.26) * mm});
            skLineSegment(sketch, "E190.top", {"start": v(-2550, 101.26) * mm, "end": v(-3100, 101.26) * mm});
            skLineSegment(sketch, "E190.left", {"start": v(-2550, 2401.26) * mm, "end": v(-2550, 101.26) * mm});
            skLineSegment(sketch, "E190.right", {"start": v(-3100, 2401.26) * mm, "end": v(-3100, 101.26) * mm});
            skLineSegment(sketch, "E191.bottom", {"start": v(-2550, 2451.26) * mm, "end": v(-3100, 2451.26) * mm});
            skLineSegment(sketch, "E191.left", {"start": v(-2550, 2451.26) * mm, "end": v(-2550, 4459.94) * mm});
            skLineSegment(sketch, "E192", {"start": v(-3100, 4281.23) * mm, "end": v(-2550, 4459.94) * mm});
            skPoint(sketch, "E193.orphan", {"position": v(-3150, 5006.8) * mm});
            skLineSegment(sketch, "E194.bottom", {"start": v(2550, 101.26) * mm, "end": v(3100, 101.26) * mm});
            skLineSegment(sketch, "E194.top", {"start": v(2550, 2401.26) * mm, "end": v(3100, 2401.26) * mm});
            skLineSegment(sketch, "E194.left", {"start": v(2550, 101.26) * mm, "end": v(2550, 2401.26) * mm});
            skLineSegment(sketch, "E194.right", {"start": v(3100, 101.26) * mm, "end": v(3100, 2401.26) * mm});
            skLineSegment(sketch, "E195.bottom", {"start": v(2550, 2451.26) * mm, "end": v(3100, 2451.26) * mm});
            skLineSegment(sketch, "E195.top", {"start": v(2550, 6728.7) * mm, "end": v(3100, 6728.7) * mm});
            skLineSegment(sketch, "E195.left", {"start": v(2550, 2451.26) * mm, "end": v(2550, 4459.94) * mm});
            skLineSegment(sketch, "E195.right", {"start": v(3100, 2451.26) * mm, "end": v(3100, 4281.23) * mm});
            skLineSegment(sketch, "E196", {"start": v(3100, 4281.23) * mm, "end": v(2550, 4459.94) * mm});
            skLineSegment(sketch, "E197", {"start": v(-3100, 2451.26) * mm, "end": v(-3100, 4281.23) * mm});
            skLineSegment(sketch, "E198", {"start": v(-2550, 4459.94) * mm, "end": v(-1850, 4687.38) * mm});
            skLineSegment(sketch, "E199", {"start": v(0, 5288.48) * mm, "end": v(150, 5239.74) * mm});
            skLineSegment(sketch, "E200.top", {"start": v(-2450, 3850) * mm, "end": v(-1850, 3850) * mm});
            skLineSegment(sketch, "E201.left", {"start": v(-1000, 3850) * mm, "end": v(-1000, 4963.56) * mm});
            skLineSegment(sketch, "E201.right", {"start": v(-1200, 3850) * mm, "end": v(-1200, 4898.58) * mm});
            skPoint(sketch, "E201.top.end.orphan", {"position": v(-1200, 5019.71) * mm});
            skLineSegment(sketch, "E202.trimOffspring", {"start": v(-1000, 3850) * mm, "end": v(-650, 3850) * mm});
            skLineSegment(sketch, "E203", {"start": v(-2450, 3850) * mm, "end": v(-2450, 4492.43) * mm});
            skLineSegment(sketch, "E204", {"start": v(2450, 3850) * mm, "end": v(2450, 4492.43) * mm});
            skLineSegment(sketch, "E205.left", {"start": v(1000, 3850) * mm, "end": v(1000, 4963.56) * mm});
            skLineSegment(sketch, "E205.right", {"start": v(1200, 3850) * mm, "end": v(1200, 4898.58) * mm});
            skPoint(sketch, "E206.orphan", {"position": v(1200, 6042.85) * mm});
            skLineSegment(sketch, "E207.trimOffspring", {"start": v(1200, 3850) * mm, "end": v(1800, 3850) * mm});
            skLineSegment(sketch, "E208", {"start": v(-1000, 4963.56) * mm, "end": v(-650, 5077.28) * mm});
            skLineSegment(sketch, "E209.left", {"start": v(-1800, 3850) * mm, "end": v(-1800, 4703.63) * mm});
            skLineSegment(sketch, "E209.right", {"start": v(-1850, 3850) * mm, "end": v(-1850, 4687.38) * mm});
            skLineSegment(sketch, "E210.left", {"start": v(1850, 3850) * mm, "end": v(1850, 4687.38) * mm});
            skLineSegment(sketch, "E210.right", {"start": v(1800, 3850) * mm, "end": v(1800, 4703.63) * mm});
            skLineSegment(sketch, "E211.trimOffspring", {"start": v(-1800, 3850) * mm, "end": v(-1200, 3850) * mm});
            skLineSegment(sketch, "E212.trimOffspring", {"start": v(-1800, 4703.63) * mm, "end": v(-650, 5077.28) * mm});
            skLineSegment(sketch, "E213.trimOffspring", {"start": v(1850, 3850) * mm, "end": v(2450, 3850) * mm});
            skLineSegment(sketch, "E214.trimOffspring", {"start": v(1850, 4687.38) * mm, "end": v(2450, 4492.43) * mm});
            skLineSegment(sketch, "E215.left", {"start": v(-600, 3850) * mm, "end": v(-600, 5093.53) * mm});
            skLineSegment(sketch, "E215.right", {"start": v(-650, 3850) * mm, "end": v(-650, 5077.28) * mm});
            skLineSegment(sketch, "E216.left", {"start": v(-200, 3850) * mm, "end": v(-200, 5223.5) * mm});
            skLineSegment(sketch, "E216.right", {"start": v(-150, 3850) * mm, "end": v(-150, 5239.74) * mm});
            skLineSegment(sketch, "E217.left", {"start": v(150, 3850) * mm, "end": v(150, 5239.74) * mm});
            skLineSegment(sketch, "E217.right", {"start": v(200, 3850) * mm, "end": v(200, 5223.5) * mm});
            skLineSegment(sketch, "E218.left", {"start": v(600, 3850) * mm, "end": v(600, 5093.53) * mm});
            skLineSegment(sketch, "E218.right", {"start": v(650, 3850) * mm, "end": v(650, 5077.28) * mm});
            skLineSegment(sketch, "E219.trimOffspring", {"start": v(-600, 5093.53) * mm, "end": v(-200, 5223.5) * mm});
            skLineSegment(sketch, "E220.trimOffspring", {"start": v(-150, 5239.74) * mm, "end": v(0, 5288.48) * mm});
            skLineSegment(sketch, "E221.trimOffspring", {"start": v(-600, 3850) * mm, "end": v(-200, 3850) * mm});
            skLineSegment(sketch, "E222.trimOffspring", {"start": v(200, 3850) * mm, "end": v(600, 3850) * mm});
            skLineSegment(sketch, "E223.trimOffspring", {"start": v(650, 3850) * mm, "end": v(1000, 3850) * mm});
            skLineSegment(sketch, "E224", {"start": v(-150, 3850) * mm, "end": v(150, 3850) * mm});
            skLineSegment(sketch, "E225.trimOffspring", {"start": v(200, 5223.5) * mm, "end": v(600, 5093.53) * mm});
            skLineSegment(sketch, "E226.trimOffspring", {"start": v(650, 5077.28) * mm, "end": v(1000, 4963.56) * mm});
            skLineSegment(sketch, "E227.trimOffspring", {"start": v(1200, 4898.58) * mm, "end": v(1800, 4703.63) * mm});
            skLineSegment(sketch, "E228.bottom", {"start": v(-2450, 2751.26) * mm, "end": v(-1200, 2751.26) * mm});
            skLineSegment(sketch, "E228.top", {"start": v(-2450, 2451.26) * mm, "end": v(-1200, 2451.26) * mm});
            skLineSegment(sketch, "E228.left", {"start": v(-2450, 2751.26) * mm, "end": v(-2450, 2451.26) * mm});
            skLineSegment(sketch, "E228.right", {"start": v(-1200, 2751.26) * mm, "end": v(-1200, 2451.26) * mm});
            skLineSegment(sketch, "E229.bottom", {"start": v(-1000, 2751.26) * mm, "end": v(1000, 2751.26) * mm});
            skLineSegment(sketch, "E229.top", {"start": v(-1000, 2451.26) * mm, "end": v(1000, 2451.26) * mm});
            skLineSegment(sketch, "E229.left", {"start": v(-1000, 2751.26) * mm, "end": v(-1000, 2451.26) * mm});
            skLineSegment(sketch, "E229.right", {"start": v(1000, 2751.26) * mm, "end": v(1000, 2451.26) * mm});
            skLineSegment(sketch, "E230.bottom", {"start": v(1200, 2751.26) * mm, "end": v(2450, 2751.26) * mm});
            skLineSegment(sketch, "E230.top", {"start": v(1200, 2451.26) * mm, "end": v(2450, 2451.26) * mm});
            skLineSegment(sketch, "E230.left", {"start": v(1200, 2751.26) * mm, "end": v(1200, 2451.26) * mm});
            skLineSegment(sketch, "E230.right", {"start": v(2450, 2751.26) * mm, "end": v(2450, 2451.26) * mm});
            skSolve(sketch);
        }
        {
            var Q0;
            Q0 = qSketchRegion(id + "F34", true);
            extrude(context, id + "F35", {"entities" : qUnion([Q0]), "operationType" : NewBodyOperationType.REMOVE, "oppositeDirection" : true, "depth" : 200 * mm, "offsetDistance" : 25 * mm});
        }
        {
            var Q0;
            Q0=makeQuery(id+"F1.opExtrude","SWEPT_FACE",FACE,{"disambiguationData":[OSD([sQuery(id+"F0.wireOp",EDGE,"E5.top"),sQuery(id+"F0.wireOp",EDGE,"E6.bottom")])]});
            var sketch = newSketch(context, id + "F36", { "sketchPlane" : qUnion([Q0])});
            skLineSegment(sketch, "E231", {"start": v(4330, 100) * mm, "end": v(4330, 299.9) * mm});
            skLineSegment(sketch, "E232", {"start": v(4330, 299.9) * mm, "end": v(3430.91, 2521.26) * mm});
            skLineSegment(sketch, "E233", {"start": v(3430.91, 2521.26) * mm, "end": v(3350, 2521.26) * mm});
            skLineSegment(sketch, "E234", {"start": v(3350, 2521.26) * mm, "end": v(3350, 2321.35) * mm});
            skLineSegment(sketch, "E235", {"start": v(3350, 2321.35) * mm, "end": v(4249.09, 100) * mm});
            skLineSegment(sketch, "E236", {"start": v(4249.09, 100) * mm, "end": v(4330, 100) * mm});
            skLineSegment(sketch, "E237", {"start": v(6470, 100) * mm, "end": v(6470, 233.27) * mm});
            skLineSegment(sketch, "E238", {"start": v(6470, 233.27) * mm, "end": v(7396.06, 2521.26) * mm});
            skLineSegment(sketch, "E239", {"start": v(7450, 2521.26) * mm, "end": v(7450, 2387.99) * mm});
            skLineSegment(sketch, "E240", {"start": v(7450, 2387.99) * mm, "end": v(6523.94, 100) * mm});
            skLineSegment(sketch, "E241", {"start": v(6523.94, 100) * mm, "end": v(6470, 100) * mm});
            skLineSegment(sketch, "E242", {"start": v(7396.06, 2521.26) * mm, "end": v(7450, 2521.26) * mm});
            skSolve(sketch);
        }
        {
            var Q0;
            Q0 = qSketchRegion(id + "F36", true);
            extrude(context, id + "F37", {"entities" : qUnion([Q0]), "oppositeDirection" : true, "depth" : 50 * mm, "offsetDistance" : 25 * mm});
        }
        {
            var Q0;
            {var subQ5=sQuery(id+"F0.wireOp",EDGE,"E1.bottom");var subQ6=makeQuery(id+"F1.opExtrude","SWEPT_FACE",FACE,{"disambiguationData":[OSD([subQ5])]});var subQ18=subQ6;Q0=makeQuery(id+"F33.boolean.opBoolean","MERGE",FACE,{"derivedFrom":[makeQuery(id+"F25.boolean.opBoolean","SPLIT",FACE,{"disambiguationData":[TD([makeQuery(id+"F15.boolean.opBoolean","COPY",FACE,{"derivedFrom":makeQuery(id+"F15.opExtrude","SWEPT_FACE",FACE,{"disambiguationData":[OSD([sQuery(id+"F14.wireOp",EDGE,"E52.right")])]})})])],"derivedFrom":subQ18}),makeQuery(id+"F25.boolean.opBoolean","SPLIT",FACE,{"disambiguationData":[TD([makeQuery(id+"F15.boolean.opBoolean","COPY",FACE,{"derivedFrom":makeQuery(id+"F15.opExtrude","SWEPT_FACE",FACE,{"disambiguationData":[OSD([sQuery(id+"F14.wireOp",EDGE,"E53.right")])]})})])],"derivedFrom":subQ18}),makeQuery(id+"F25.boolean.opBoolean","SPLIT",FACE,{"disambiguationData":[TD([makeQuery(id+"F15.boolean.opBoolean","COPY",FACE,{"derivedFrom":makeQuery(id+"F15.opExtrude","SWEPT_FACE",FACE,{"disambiguationData":[OSD([sQuery(id+"F14.wireOp",EDGE,"E54.bottom")])]})})])],"derivedFrom":subQ18}),makeQuery(id+"F33.opExtrude","CAP_FACE",FACE,{"disambiguationData":[OSD([sQuery(id+"F32.wireOp",EDGE,"E186.bottom"),sQuery(id+"F32.wireOp",EDGE,"E186.top"),sQuery(id+"F32.wireOp",EDGE,"E186.left"),sQuery(id+"F32.wireOp",EDGE,"E186.right")])],"isStart":true})]});}
            var sketch = newSketch(context, id + "F38", { "sketchPlane" : qUnion([Q0])});
            skLineSegment(sketch, "E243", {"start": v(-2550, 101.26) * mm, "end": v(-2550, 423.73) * mm});
            skLineSegment(sketch, "E244", {"start": v(-2550, 423.73) * mm, "end": v(-3022.89, 2401.26) * mm});
            skLineSegment(sketch, "E245", {"start": v(-3022.89, 2401.26) * mm, "end": v(-3100, 2401.26) * mm});
            skLineSegment(sketch, "E246", {"start": v(-3100, 2401.26) * mm, "end": v(-3100, 2078.78) * mm});
            skLineSegment(sketch, "E247", {"start": v(-3100, 2078.78) * mm, "end": v(-2627.11, 101.26) * mm});
            skLineSegment(sketch, "E248", {"start": v(-2627.11, 101.26) * mm, "end": v(-2550, 101.26) * mm});
            skLineSegment(sketch, "E249", {"start": v(3100, 2401.26) * mm, "end": v(3022.89, 2401.26) * mm});
            skLineSegment(sketch, "E250", {"start": v(3022.89, 2401.26) * mm, "end": v(2550, 423.73) * mm});
            skLineSegment(sketch, "E251", {"start": v(2550, 423.73) * mm, "end": v(2550, 101.26) * mm});
            skLineSegment(sketch, "E252", {"start": v(2550, 101.26) * mm, "end": v(2627.11, 101.26) * mm});
            skLineSegment(sketch, "E253", {"start": v(2627.11, 101.26) * mm, "end": v(3100, 2078.78) * mm});
            skLineSegment(sketch, "E254", {"start": v(3100, 2078.78) * mm, "end": v(3100, 2401.26) * mm});
            skLineSegment(sketch, "E255", {"start": v(-3100, 4281.23) * mm, "end": v(-3100, 4020.66) * mm});
            skLineSegment(sketch, "E256", {"start": v(-3100, 4020.66) * mm, "end": v(-2628.31, 2451.26) * mm});
            skLineSegment(sketch, "E257", {"start": v(-2628.31, 2451.26) * mm, "end": v(-2550, 2451.26) * mm});
            skLineSegment(sketch, "E258", {"start": v(-2550, 2451.26) * mm, "end": v(-2550, 2711.82) * mm});
            skLineSegment(sketch, "E259", {"start": v(-3100, 4281.23) * mm, "end": v(0, 5290.63) * mm});
            skLineSegment(sketch, "E260", {"start": v(-2550, 2711.82) * mm, "end": v(-3028.67, 4304.46) * mm});
            skLineSegment(sketch, "E261", {"start": v(3100, 4281.23) * mm, "end": v(3100, 4020.66) * mm});
            skLineSegment(sketch, "E262", {"start": v(3100, 4020.66) * mm, "end": v(2628.31, 2451.26) * mm});
            skLineSegment(sketch, "E263", {"start": v(2628.31, 2451.26) * mm, "end": v(2550, 2451.26) * mm});
            skLineSegment(sketch, "E264", {"start": v(2550, 2451.26) * mm, "end": v(2550, 2711.82) * mm});
            skLineSegment(sketch, "E265", {"start": v(2550, 2711.82) * mm, "end": v(3028.86, 4305.1) * mm});
            skLineSegment(sketch, "E266", {"start": v(3028.86, 4305.1) * mm, "end": v(3100, 4281.23) * mm});
            skLineSegment(sketch, "E267", {"start": v(3100, 4020.66) * mm, "end": v(3100, 4281.23) * mm});
            skLineSegment(sketch, "E268.bottom", {"start": v(-84.22, 5090.63) * mm, "end": v(84.22, 5090.63) * mm});
            skPoint(sketch, "E268.middle", {"position": v(0, 5290.63) * mm});
            skLineSegment(sketch, "E269", {"start": v(1000, 3850) * mm, "end": v(1000, 3969.51) * mm});
            skLineSegment(sketch, "E270", {"start": v(1000, 3969.51) * mm, "end": v(96.33, 5090.63) * mm});
            skLineSegment(sketch, "E271", {"start": v(-96.33, 5090.63) * mm, "end": v(-1000, 3969.51) * mm});
            skLineSegment(sketch, "E272", {"start": v(-1000, 3969.51) * mm, "end": v(-1000, 3850) * mm});
            skLineSegment(sketch, "E273", {"start": v(-1000, 3850) * mm, "end": v(-903.67, 3850) * mm});
            skLineSegment(sketch, "E274", {"start": v(-903.67, 3850) * mm, "end": v(0, 4971.12) * mm});
            skLineSegment(sketch, "E275", {"start": v(0, 4971.12) * mm, "end": v(903.67, 3850) * mm});
            skLineSegment(sketch, "E276", {"start": v(903.67, 3850) * mm, "end": v(1000, 3850) * mm});
            skPoint(sketch, "E277.start.orphan", {"position": v(0, 5090.63) * mm});
            skLineSegment(sketch, "E278", {"start": v(84.22, 5090.63) * mm, "end": v(96.33, 5090.63) * mm});
            skLineSegment(sketch, "E279", {"start": v(-84.22, 5090.63) * mm, "end": v(-96.33, 5090.63) * mm});
            skPoint(sketch, "E280.orphan", {"position": v(-84.22, 5490.63) * mm});
            skPoint(sketch, "E281.orphan", {"position": v(84.22, 5490.63) * mm});
            skSolve(sketch);
        }
        {
            var Q0;
            Q0 = qSketchRegion(id + "F38", true);
            extrude(context, id + "F39", {"entities" : qUnion([Q0]), "oppositeDirection" : true, "depth" : 50 * mm, "offsetDistance" : 25 * mm});
        }
        {
            var Q0;
            Q0=makeQuery(id+"F39.opExtrude","CAP_FACE",FACE,{"disambiguationData":[OSD([sQuery(id+"F38.wireOp",EDGE,"E268.bottom"),sQuery(id+"F38.wireOp",EDGE,"E269"),sQuery(id+"F38.wireOp",EDGE,"E270"),sQuery(id+"F38.wireOp",EDGE,"E271"),sQuery(id+"F38.wireOp",EDGE,"E272"),sQuery(id+"F38.wireOp",EDGE,"E273"),sQuery(id+"F38.wireOp",EDGE,"E274"),sQuery(id+"F38.wireOp",EDGE,"E275"),sQuery(id+"F38.wireOp",EDGE,"E276"),sQuery(id+"F38.wireOp",EDGE,"E278"),sQuery(id+"F38.wireOp",EDGE,"E279")])],"isStart":true});
            var sketch = newSketch(context, id + "F40", { "sketchPlane" : qUnion([Q0])});
            skLineSegment(sketch, "E282.top", {"start": v(-50, 5099.7) * mm, "end": v(50, 5099.7) * mm});
            skLineSegment(sketch, "E282.left", {"start": v(-50, 5272.67) * mm, "end": v(-50, 5099.7) * mm});
            skLineSegment(sketch, "E282.right", {"start": v(50, 5272.67) * mm, "end": v(50, 5099.7) * mm});
            skPoint(sketch, "E282.middle", {"position": v(0, 5199.7) * mm});
            skPoint(sketch, "E282.middle.positionSnap0", {"position": v(0, 5090.63) * mm});
            skPoint(sketch, "E282.centerSnap0", {"position": v(0, 5090.63) * mm});
            skLineSegment(sketch, "E283", {"start": v(0, 5288.46) * mm, "end": v(50, 5272.67) * mm});
            skLineSegment(sketch, "E284", {"start": v(-50, 5272.67) * mm, "end": v(0, 5288.46) * mm});
            skPoint(sketch, "E282.bottom.end.orphan", {"position": v(50, 5299.7) * mm});
            skPoint(sketch, "E285.orphan", {"position": v(-50, 5299.7) * mm});
            skSolve(sketch);
        }
        {
            var Q0;
            Q0 = qSketchRegion(id + "F40", true);
            extrude(context, id + "F41", {"entities" : qUnion([Q0]), "oppositeDirection" : true, "depth" : 10200 * mm, "offsetDistance" : 25 * mm});
        }
        {
            var Q0;
            Q0=makeQuery(id+"F21.opExtrude","SWEPT_FACE",FACE,{"disambiguationData":[OSD([sQuery(id+"F20.wireOp",EDGE,"E66.bottom")])]});
            var sketch = newSketch(context, id + "F42", { "sketchPlane" : qUnion([Q0])});
            skLineSegment(sketch, "E286", {"start": v(0, 5478.7) * mm, "end": v(0, 5288.48) * mm});
            skLineSegment(sketch, "E287", {"start": v(-61.8, 5478.7) * mm, "end": v(0, 5498.77) * mm});
            skLineSegment(sketch, "E288", {"start": v(0, 5478.7) * mm, "end": v(0, 5498.77) * mm});
            skLineSegment(sketch, "E289", {"start": v(-61.8, 5478.7) * mm, "end": v(0, 5288.48) * mm});
            skSolve(sketch);
        }
        {
            var Q0;
            Q0 = qSketchRegion(id + "F42", true);
            extrude(context, id + "F43", {"entities" : qUnion([Q0]), "operationType" : NewBodyOperationType.ADD, "oppositeDirection" : true, "depth" : 50 * mm, "offsetDistance" : 25 * mm});
        }
        {
            var Q0;
            Q0=makeQuery(id+"F23.opExtrude","SWEPT_FACE",FACE,{"disambiguationData":[OSD([sQuery(id+"F22.wireOp",EDGE,"E67.bottom")])]});
            var sketch = newSketch(context, id + "F44", { "sketchPlane" : qUnion([Q0])});
            skLineSegment(sketch, "E290", {"start": v(61.8, 5478.7) * mm, "end": v(0, 5288.48) * mm});
            skLineSegment(sketch, "E291", {"start": v(61.8, 5478.7) * mm, "end": v(0, 5498.77) * mm});
            skLineSegment(sketch, "E292", {"start": v(0, 5498.77) * mm, "end": v(0, 5288.48) * mm});
            skSolve(sketch);
        }
        {
            var Q0;
            Q0 = qSketchRegion(id + "F44", true);
            extrude(context, id + "F45", {"entities" : qUnion([Q0]), "operationType" : NewBodyOperationType.ADD, "oppositeDirection" : true, "depth" : 50 * mm, "offsetDistance" : 25 * mm});
        }
    });
